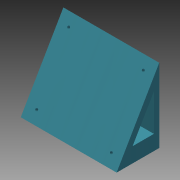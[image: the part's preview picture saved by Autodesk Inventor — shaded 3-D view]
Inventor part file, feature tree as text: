
AUTODESK INVENTOR PART (.ipt)
format: ipt  version: 2013 (Build 170138000, 138)  size: 123,904 bytes
history: native  units: mm
features: sketch x4, extrude x2, hole x2, other x1
ambient origin geometry x8: Origin, YZ Plane, XZ Plane, XY Plane, X Axis, Y Axis, Z Axis, Center Point
feature tree (9):
  other  "ソリッド1"
  extrude  "押し出し1"  Depth=80.0mm
  hole  "穴1"  [1 undecoded]
  hole  "穴2"  [1 undecoded]
  extrude  "押し出し2"  Depth=90.0mm TaperAngle=0.0deg
  sketch  "スケッチ1"
  sketch  "スケッチ2"
  sketch  "スケッチ3"
  sketch  "スケッチ4"
note: 2 required parameter values undecoded (feature->parameter linkage not recoverable at this tier; creation-order binding heuristic only, values carry confidence <= 0.55)
